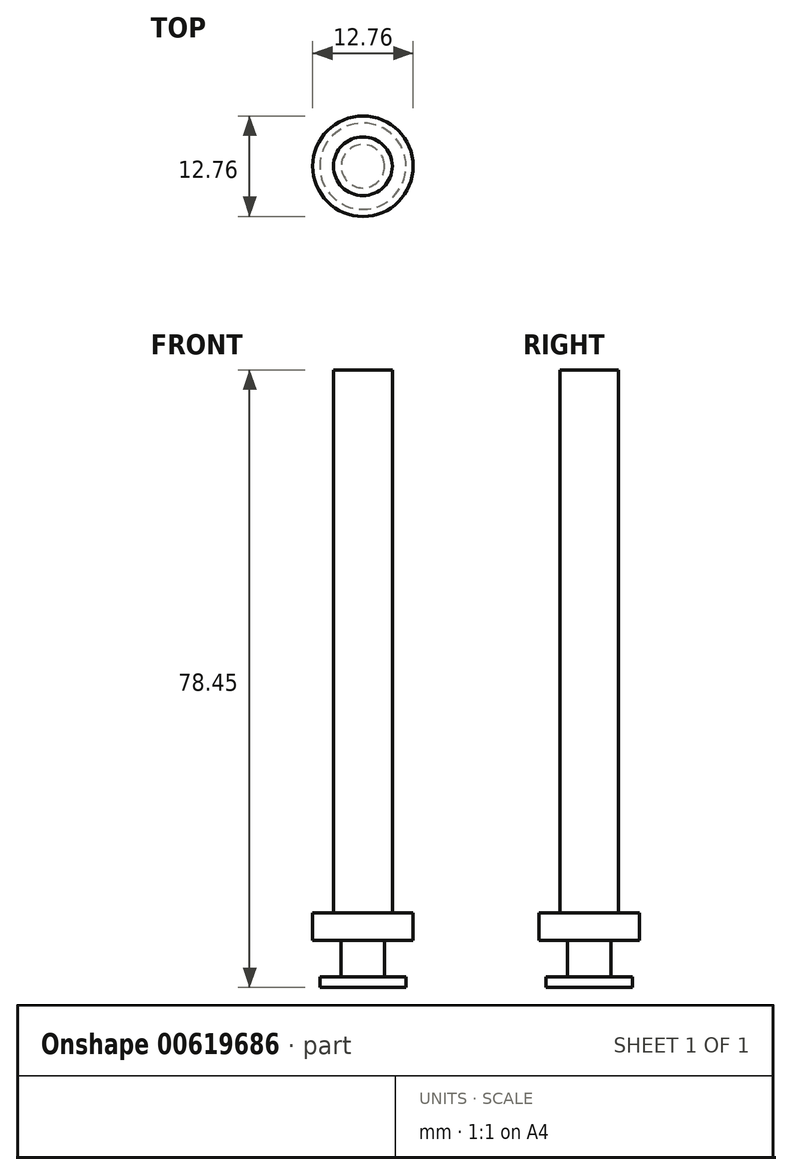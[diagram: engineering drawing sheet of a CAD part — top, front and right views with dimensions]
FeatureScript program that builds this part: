
annotation { "Feature Type Name" : "Feature", "Feature Type Description" : "" }
export const myFeature = defineFeature(function(context is Context, id is Id, definition is map)
    precondition{}
    {
        {
            var Q0;
            Q0=qCreatedBy(makeId("Top.planeOp"),FACE);
            var sketch = newSketch(context, id + "F0", { "sketchPlane" : qUnion([Q0])});
            skCircle(sketch, "E0", {"center": v(0, 0) * mm, "radius": 5.47 * mm});
            skSolve(sketch);
        }
        {
            var Q0;
            Q0 = qSketchRegion(id + "F0", true);
            extrude(context, id + "F1", {"entities" : qUnion([Q0]), "depth" : 1.35 * mm, "offsetDistance" : 25 * mm});
        }
        {
            var Q0;
            Q0=qCreatedBy(makeId("Top.planeOp"),FACE);
            var sketch = newSketch(context, id + "F2", { "sketchPlane" : qUnion([Q0])});
            skCircle(sketch, "E1", {"center": v(0, 0) * mm, "radius": 2.75 * mm});
            skSolve(sketch);
        }
        {
            var Q0;
            Q0 = qSketchRegion(id + "F2", true);
            extrude(context, id + "F3", {"entities" : qUnion([Q0]), "operationType" : NewBodyOperationType.ADD, "depth" : 6 * mm, "offsetDistance" : 25 * mm});
        }
        {
            var Q0;
            Q0=makeQuery(id+"F3.opExtrude","CAP_FACE",FACE,{"disambiguationData":[OSD([sQuery(id+"F2.wireOp",EDGE,"E1")])],"isStart":false});
            var sketch = newSketch(context, id + "F4", { "sketchPlane" : qUnion([Q0])});
            skCircle(sketch, "E2", {"center": v(0, 0) * mm, "radius": 6.38 * mm});
            skSolve(sketch);
        }
        {
            var Q0;
            Q0 = qSketchRegion(id + "F4", true);
            extrude(context, id + "F5", {"entities" : qUnion([Q0]), "operationType" : NewBodyOperationType.ADD, "depth" : 3.45 * mm, "offsetDistance" : 25 * mm});
        }
        {
            var Q0;
            Q0=makeQuery(id+"F5.opExtrude","CAP_FACE",FACE,{"disambiguationData":[OSD([sQuery(id+"F4.wireOp",EDGE,"E2")])],"isStart":false});
            var sketch = newSketch(context, id + "F6", { "sketchPlane" : qUnion([Q0])});
            skCircle(sketch, "E3", {"center": v(0, 0) * mm, "radius": 3.73 * mm});
            skSolve(sketch);
        }
        {
            var Q0;
            Q0 = qSketchRegion(id + "F6", true);
            extrude(context, id + "F7", {"entities" : qUnion([Q0]), "operationType" : NewBodyOperationType.ADD, "depth" : 69 * mm, "offsetDistance" : 25 * mm});
        }
    });
